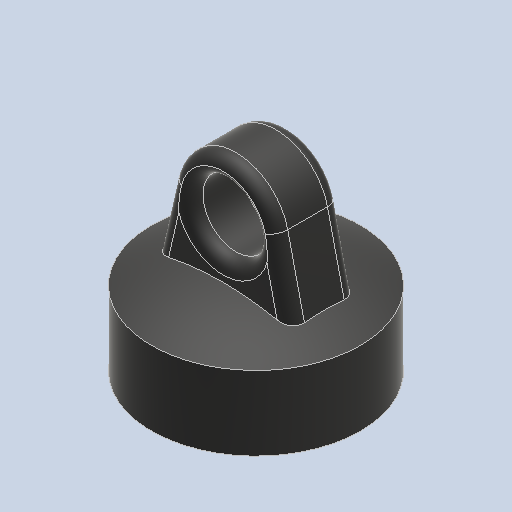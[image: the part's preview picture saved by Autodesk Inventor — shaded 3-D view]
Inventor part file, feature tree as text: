
AUTODESK INVENTOR PART (.ipt)
format: ipt  version: 2023 (Build 270158030, 158C)  size: 199,680 bytes
history: native  units: mm
features: sketch x4, extrude x3, other x1, revolve x1, fillet x1
ambient origin geometry x8: Origin, YZ Plane, XZ Plane, XY Plane, X Axis, Y Axis, Z Axis, Center Point
bodies: Body1 (feature_tree), Body2 (feature_tree)
feature tree (10):
  other  "ソリッド1"
  extrude  "押し出し1"  Depth=15.75mm
  extrude  "押し出し2"  Depth=5.6mm TaperAngle=0.0deg
  revolve  "回転1"
  extrude  "押し出し3"  Depth=5.0mm
  fillet  "フィレット1"  Radius=1.5mm
  sketch  "スケッチ1"
  sketch  "スケッチ2"
  sketch  "スケッチ3"
  sketch  "スケッチ4"
